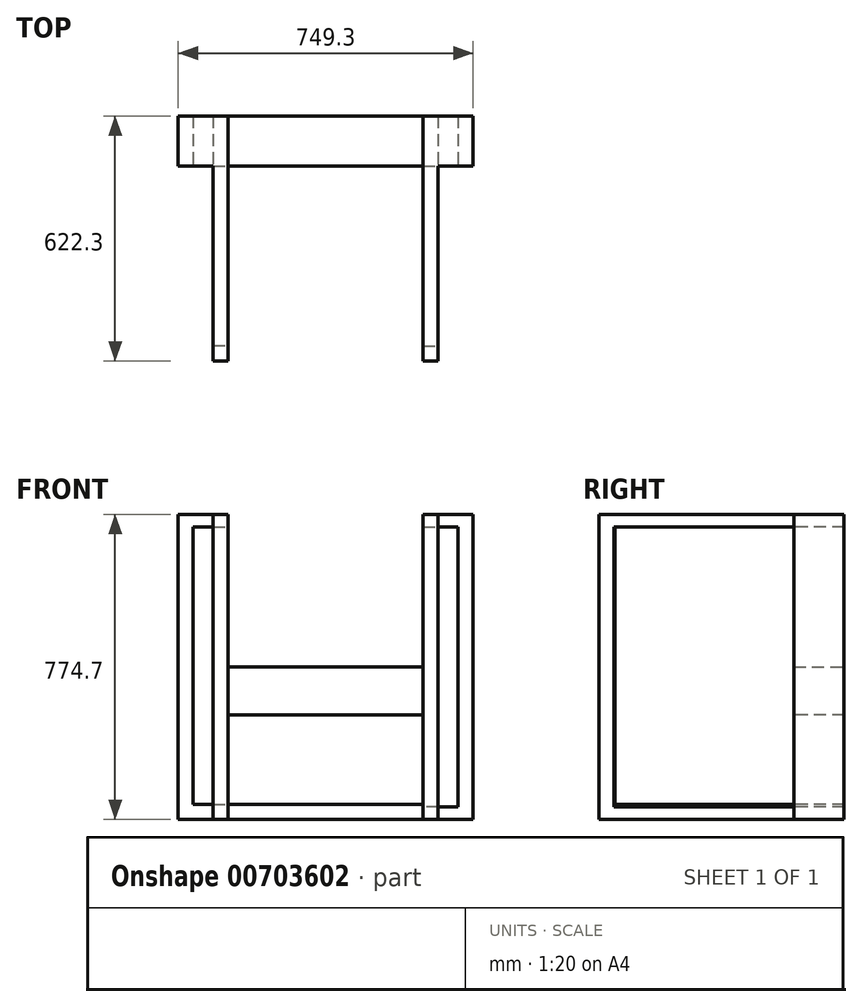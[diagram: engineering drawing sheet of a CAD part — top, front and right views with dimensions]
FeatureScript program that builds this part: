
annotation { "Feature Type Name" : "Feature", "Feature Type Description" : "" }
export const myFeature = defineFeature(function(context is Context, id is Id, definition is map)
    precondition{}
    {
        {
            var Q0;
            Q0=qCreatedBy(makeId("Front.planeOp"),FACE);
            var sketch = newSketch(context, id + "F0", { "sketchPlane" : qUnion([Q0])});
            skLineSegment(sketch, "E0.bottom", {"start": v(-354.39, 388.76) * mm, "end": v(394.91, 388.76) * mm});
            skLineSegment(sketch, "E0.top", {"start": v(-354.39, -385.94) * mm, "end": v(394.91, -385.94) * mm});
            skLineSegment(sketch, "E0.left", {"start": v(-354.39, 388.76) * mm, "end": v(-354.39, -385.94) * mm});
            skLineSegment(sketch, "E0.right", {"start": v(394.91, 388.76) * mm, "end": v(394.91, -385.94) * mm});
            skLineSegment(sketch, "E1.bottom", {"start": v(-227.39, 388.76) * mm, "end": v(267.91, 388.76) * mm});
            skLineSegment(sketch, "E1.top", {"start": v(-227.39, 1.4) * mm, "end": v(267.91, 1.4) * mm});
            skLineSegment(sketch, "E1.left", {"start": v(-227.39, 388.76) * mm, "end": v(-227.39, 1.4) * mm});
            skLineSegment(sketch, "E1.right", {"start": v(267.91, 388.76) * mm, "end": v(267.91, 1.4) * mm});
            skSolve(sketch);
        }
        {
            var Q0;
            Q0=makeQuery(id+"F0.imprint","IMPRINT",FACE,{"disambiguationData":[TD([[makeQuery(id+"F0.imprint","IMPRINT",EDGE,{"derivedFrom":sQuery(id+"F0.wireOp",EDGE,"E0.top")}),1.0]])]});
            extrude(context, id + "F1", {"entities" : qUnion([Q0]), "depth" : 127 * mm, "offsetDistance" : 25.4 * mm});
        }
        {
            var Q0;
            Q0=makeQuery(id+"F1.opExtrude","CAP_FACE",FACE,{"disambiguationData":[OSD([sQuery(id+"F0.wireOp",EDGE,"E0.bottom"),sQuery(id+"F0.wireOp",EDGE,"E0.top"),sQuery(id+"F0.wireOp",EDGE,"E0.left"),sQuery(id+"F0.wireOp",EDGE,"E0.right"),sQuery(id+"F0.wireOp",EDGE,"E1.top"),sQuery(id+"F0.wireOp",EDGE,"E1.left"),sQuery(id+"F0.wireOp",EDGE,"E1.right")])],"isStart":false});
            var sketch = newSketch(context, id + "F2", { "sketchPlane" : qUnion([Q0])});
            skLineSegment(sketch, "E2.bottom", {"start": v(-316.29, 357) * mm, "end": v(-265.49, 357) * mm});
            skLineSegment(sketch, "E2.top", {"start": v(-316.29, -347.72) * mm, "end": v(-265.49, -347.72) * mm});
            skLineSegment(sketch, "E2.left", {"start": v(-316.29, 357) * mm, "end": v(-316.29, -347.72) * mm});
            skLineSegment(sketch, "E2.right", {"start": v(-265.49, 357) * mm, "end": v(-265.49, -347.72) * mm});
            skSolve(sketch);
        }
        {
            var Q0;
            Q0=makeQuery(id+"F2.imprint","IMPRINT",FACE,{"disambiguationData":[TD([[makeQuery(id+"F2.imprint","IMPRINT",EDGE,{"derivedFrom":sQuery(id+"F2.wireOp",EDGE,"E2.bottom")}),-1.0]])]});
            extrude(context, id + "F3", {"entities" : qUnion([Q0]), "operationType" : NewBodyOperationType.REMOVE, "oppositeDirection" : true, "depth" : 127 * mm, "offsetDistance" : 25.4 * mm});
        }
        {
            var Q0;
            Q0=makeQuery(id+"F1.opExtrude","CAP_FACE",FACE,{"disambiguationData":[OSD([sQuery(id+"F0.wireOp",EDGE,"E0.bottom"),sQuery(id+"F0.wireOp",EDGE,"E0.top"),sQuery(id+"F0.wireOp",EDGE,"E0.left"),sQuery(id+"F0.wireOp",EDGE,"E0.right"),sQuery(id+"F0.wireOp",EDGE,"E1.top"),sQuery(id+"F0.wireOp",EDGE,"E1.left"),sQuery(id+"F0.wireOp",EDGE,"E1.right")])],"isStart":false});
            var sketch = newSketch(context, id + "F4", { "sketchPlane" : qUnion([Q0])});
            skLineSegment(sketch, "E3.bottom", {"start": v(306.01, 357) * mm, "end": v(356.81, 357) * mm});
            skLineSegment(sketch, "E3.top", {"start": v(306.01, -354.2) * mm, "end": v(356.81, -354.2) * mm});
            skLineSegment(sketch, "E3.left", {"start": v(306.01, 357) * mm, "end": v(306.01, -354.2) * mm});
            skLineSegment(sketch, "E3.right", {"start": v(356.81, 357) * mm, "end": v(356.81, -354.2) * mm});
            skSolve(sketch);
        }
        {
            var Q0;
            Q0=makeQuery(id+"F4.imprint","IMPRINT",FACE,{"disambiguationData":[TD([[makeQuery(id+"F4.imprint","IMPRINT",EDGE,{"derivedFrom":sQuery(id+"F4.wireOp",EDGE,"E3.bottom")}),-1.0]])]});
            extrude(context, id + "F5", {"entities" : qUnion([Q0]), "operationType" : NewBodyOperationType.REMOVE, "oppositeDirection" : true, "depth" : 127 * mm, "offsetDistance" : 25.4 * mm});
        }
        {
            var Q0;
            Q0=makeQuery(id+"F1.opExtrude","CAP_FACE",FACE,{"disambiguationData":[OSD([sQuery(id+"F0.wireOp",EDGE,"E0.bottom"),sQuery(id+"F0.wireOp",EDGE,"E0.top"),sQuery(id+"F0.wireOp",EDGE,"E0.left"),sQuery(id+"F0.wireOp",EDGE,"E0.right"),sQuery(id+"F0.wireOp",EDGE,"E1.top"),sQuery(id+"F0.wireOp",EDGE,"E1.left"),sQuery(id+"F0.wireOp",EDGE,"E1.right")])],"isStart":false});
            var sketch = newSketch(context, id + "F6", { "sketchPlane" : qUnion([Q0])});
            skLineSegment(sketch, "E4.bottom", {"start": v(-227.39, -120.13) * mm, "end": v(267.91, -120.13) * mm});
            skLineSegment(sketch, "E4.top", {"start": v(-227.39, -347.84) * mm, "end": v(267.91, -347.84) * mm});
            skLineSegment(sketch, "E4.left", {"start": v(-227.39, -120.13) * mm, "end": v(-227.39, -347.84) * mm});
            skLineSegment(sketch, "E4.right", {"start": v(267.91, -120.13) * mm, "end": v(267.91, -347.84) * mm});
            skSolve(sketch);
        }
        {
            var Q0;
            Q0=makeQuery(id+"F6.imprint","IMPRINT",FACE,{"disambiguationData":[TD([[makeQuery(id+"F6.imprint","IMPRINT",EDGE,{"derivedFrom":sQuery(id+"F6.wireOp",EDGE,"E4.bottom")}),-1.0]])]});
            extrude(context, id + "F7", {"entities" : qUnion([Q0]), "operationType" : NewBodyOperationType.REMOVE, "oppositeDirection" : true, "depth" : 127 * mm, "offsetDistance" : 25.4 * mm});
        }
        {
            var Q0;
            Q0=makeQuery(id+"F1.opExtrude","CAP_FACE",FACE,{"disambiguationData":[OSD([sQuery(id+"F0.wireOp",EDGE,"E0.bottom"),sQuery(id+"F0.wireOp",EDGE,"E0.top"),sQuery(id+"F0.wireOp",EDGE,"E0.left"),sQuery(id+"F0.wireOp",EDGE,"E0.right"),sQuery(id+"F0.wireOp",EDGE,"E1.top"),sQuery(id+"F0.wireOp",EDGE,"E1.left"),sQuery(id+"F0.wireOp",EDGE,"E1.right")])],"isStart":false});
            var sketch = newSketch(context, id + "F8", { "sketchPlane" : qUnion([Q0])});
            skLineSegment(sketch, "E5.bottom", {"start": v(-265.49, 357) * mm, "end": v(-227.39, 357) * mm});
            skLineSegment(sketch, "E5.top", {"start": v(-265.49, 388.76) * mm, "end": v(-227.39, 388.76) * mm});
            skLineSegment(sketch, "E5.left", {"start": v(-265.49, 357) * mm, "end": v(-265.49, 388.76) * mm});
            skLineSegment(sketch, "E5.right", {"start": v(-227.39, 357) * mm, "end": v(-227.39, 388.76) * mm});
            skLineSegment(sketch, "E6.bottom", {"start": v(267.91, 388.76) * mm, "end": v(306.01, 388.76) * mm});
            skLineSegment(sketch, "E6.top", {"start": v(267.91, 357) * mm, "end": v(306.01, 357) * mm});
            skLineSegment(sketch, "E6.left", {"start": v(267.91, 388.76) * mm, "end": v(267.91, 357) * mm});
            skLineSegment(sketch, "E6.right", {"start": v(306.01, 388.76) * mm, "end": v(306.01, 357) * mm});
            skLineSegment(sketch, "E7.bottom", {"start": v(306.01, -354.2) * mm, "end": v(267.91, -354.2) * mm});
            skLineSegment(sketch, "E7.top", {"start": v(306.01, -385.94) * mm, "end": v(267.91, -385.94) * mm});
            skLineSegment(sketch, "E7.left", {"start": v(306.01, -354.2) * mm, "end": v(306.01, -385.94) * mm});
            skLineSegment(sketch, "E7.right", {"start": v(267.91, -354.2) * mm, "end": v(267.91, -385.94) * mm});
            skLineSegment(sketch, "E8.bottom", {"start": v(-265.49, -347.72) * mm, "end": v(-227.39, -347.72) * mm});
            skLineSegment(sketch, "E8.top", {"start": v(-265.49, -385.94) * mm, "end": v(-227.39, -385.94) * mm});
            skLineSegment(sketch, "E8.left", {"start": v(-265.49, -347.72) * mm, "end": v(-265.49, -385.94) * mm});
            skLineSegment(sketch, "E8.right", {"start": v(-227.39, -347.72) * mm, "end": v(-227.39, -385.94) * mm});
            skSolve(sketch);
        }
        {
            var Q0;
            Q0=makeQuery(id+"F8.imprint","IMPRINT",FACE,{"disambiguationData":[TD([[makeQuery(id+"F8.imprint","IMPRINT",EDGE,{"derivedFrom":sQuery(id+"F8.wireOp",EDGE,"E5.bottom")}),1.0]])]});
            var Q1;
            Q1=makeQuery(id+"F8.imprint","IMPRINT",FACE,{"disambiguationData":[TD([[makeQuery(id+"F8.imprint","IMPRINT",EDGE,{"derivedFrom":sQuery(id+"F8.wireOp",EDGE,"E6.bottom")}),-1.0]])]});
            var Q2;
            Q2=makeQuery(id+"F8.imprint","IMPRINT",FACE,{"disambiguationData":[TD([[makeQuery(id+"F8.imprint","IMPRINT",EDGE,{"derivedFrom":sQuery(id+"F8.wireOp",EDGE,"E7.bottom")}),1.0]])]});
            var Q3;
            {var subQ3=sQuery(id+"F8.wireOp",EDGE,"E8.bottom");Q3=makeQuery(id+"F8.imprint","IMPRINT",FACE,{"disambiguationData":[TD([[makeQuery(id+"F8.imprint","IMPRINT",EDGE,{"derivedFrom":subQ3}),-1.0]])]});}
            extrude(context, id + "F9", {"entities" : qUnion([Q0, Q1, Q2, Q3]), "operationType" : NewBodyOperationType.ADD, "depth" : 495.3 * mm, "offsetDistance" : 25.4 * mm});
        }
        {
            var Q0;
            Q0=makeQuery(id+"F9.opExtrude","SWEPT_FACE",FACE,{"disambiguationData":[OSD([sQuery(id+"F8.wireOp",EDGE,"E5.bottom")])]});
            var sketch = newSketch(context, id + "F10", { "sketchPlane" : qUnion([Q0])});
            skLineSegment(sketch, "E9.bottom", {"start": v(-265.49, 622.3) * mm, "end": v(-227.39, 622.3) * mm});
            skLineSegment(sketch, "E9.top", {"start": v(-265.49, 582.55) * mm, "end": v(-227.39, 582.55) * mm});
            skLineSegment(sketch, "E9.left", {"start": v(-265.49, 622.3) * mm, "end": v(-265.49, 582.55) * mm});
            skLineSegment(sketch, "E9.right", {"start": v(-227.39, 622.3) * mm, "end": v(-227.39, 582.55) * mm});
            skSolve(sketch);
        }
        {
            var Q0;
            Q0=makeQuery(id+"F10.imprint","IMPRINT",FACE,{"disambiguationData":[TD([[makeQuery(id+"F10.imprint","IMPRINT",EDGE,{"derivedFrom":sQuery(id+"F10.wireOp",EDGE,"E9.bottom")}),-1.0]])]});
            extrude(context, id + "F11", {"entities" : qUnion([Q0]), "operationType" : NewBodyOperationType.ADD, "depth" : 736.6 * mm, "offsetDistance" : 25.4 * mm});
        }
        {
            var Q0;
            Q0=makeQuery(id+"F9.opExtrude","SWEPT_FACE",FACE,{"disambiguationData":[OSD([sQuery(id+"F8.wireOp",EDGE,"E6.top")])]});
            var sketch = newSketch(context, id + "F12", { "sketchPlane" : qUnion([Q0])});
            skLineSegment(sketch, "E10.bottom", {"start": v(267.91, 622.3) * mm, "end": v(306.01, 622.3) * mm});
            skLineSegment(sketch, "E10.top", {"start": v(267.91, 584.32) * mm, "end": v(306.01, 584.32) * mm});
            skLineSegment(sketch, "E10.left", {"start": v(267.91, 622.3) * mm, "end": v(267.91, 584.32) * mm});
            skLineSegment(sketch, "E10.right", {"start": v(306.01, 622.3) * mm, "end": v(306.01, 584.32) * mm});
            skSolve(sketch);
        }
        {
            var Q0;
            Q0=makeQuery(id+"F12.imprint","IMPRINT",FACE,{"disambiguationData":[TD([[makeQuery(id+"F12.imprint","IMPRINT",EDGE,{"derivedFrom":sQuery(id+"F12.wireOp",EDGE,"E10.bottom")}),-1.0]])]});
            extrude(context, id + "F13", {"entities" : qUnion([Q0]), "operationType" : NewBodyOperationType.ADD, "depth" : 736.6 * mm, "offsetDistance" : 25.4 * mm});
        }
    });
